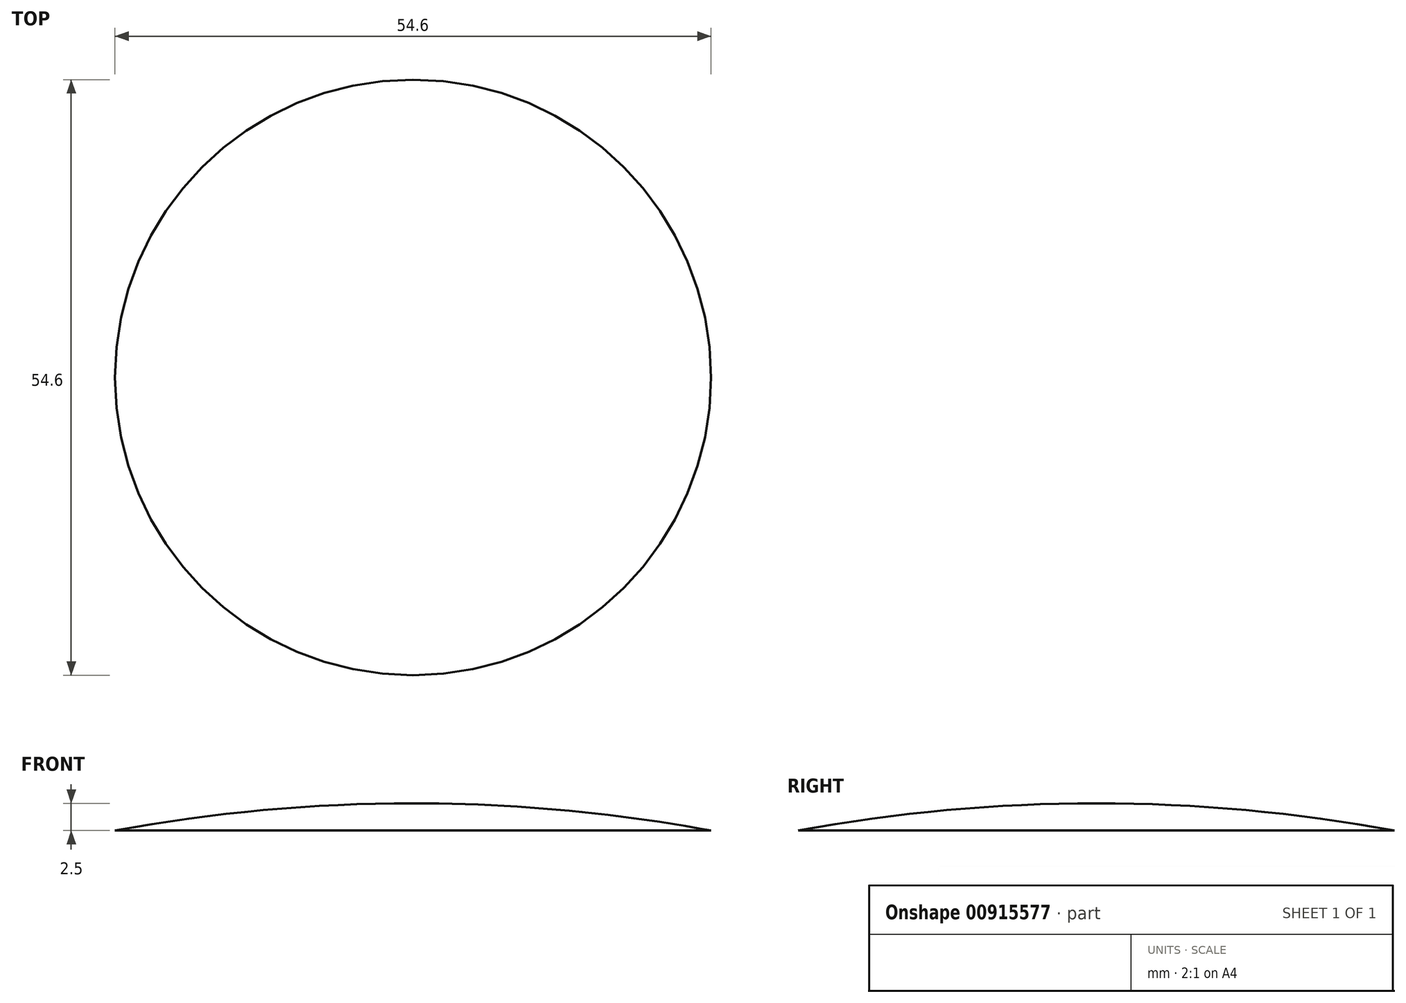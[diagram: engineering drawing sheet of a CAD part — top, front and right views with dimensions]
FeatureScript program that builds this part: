
annotation { "Feature Type Name" : "Feature", "Feature Type Description" : "" }
export const myFeature = defineFeature(function(context is Context, id is Id, definition is map)
    precondition{}
    {
        {
            var Q0;
            Q0=qCreatedBy(makeId("Front.planeOp"),FACE);
            var sketch = newSketch(context, id + "F0", { "sketchPlane" : qUnion([Q0])});
            skLineSegment(sketch, "E0", {"start": v(0, 0) * mm, "end": v(54.6, 0) * mm});
            skArc(sketch, "E1", {"start": v(54.6, 0) * mm, "mid": v(27.3, 2.5) * mm, "end": v(0, 0) * mm});
            skLineSegment(sketch, "E2", {"start": v(27.3, 0) * mm, "end": v(27.3, 2.5) * mm});
            skSolve(sketch);
        }
        {
            var Q0;
            {var subQ3=sQuery(id+"F0.wireOp",EDGE,"E2");Q0=makeQuery(id+"F0.imprint","IMPRINT",FACE,{"disambiguationData":[TD([[makeQuery(id+"F0.imprint","IMPRINT",EDGE,{"derivedFrom":subQ3}),-1.0]])]});}
            var Q1;
            Q1=sQuery(id+"F0.wireOp",EDGE,"E2");
            revolve(context, id + "F1", {"surfaceOperationType" : NewSurfaceOperationType.NEW, "entities" : qUnion([Q0]), "axis" : qUnion([Q1]), "revolveType" : RevolveType.FULL});
        }
    });
